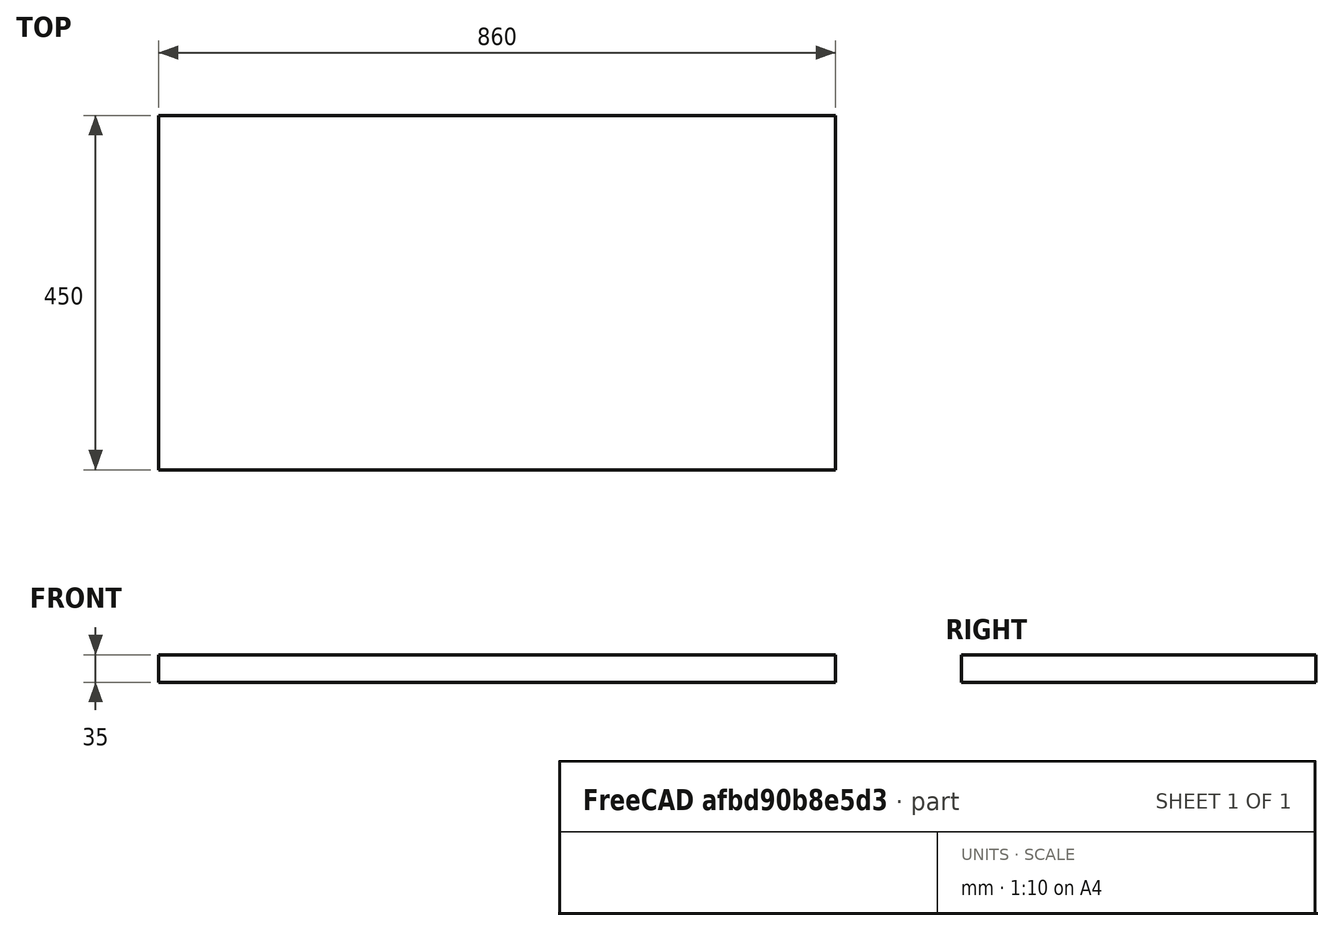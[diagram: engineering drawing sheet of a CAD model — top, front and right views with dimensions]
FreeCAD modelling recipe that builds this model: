
FCSTD DOCUMENT  (FreeCAD 0.18R4 (GitTag))
Label: benchtop_interior
License: All rights reserved
LicenseURL: http://en.wikipedia.org/wiki/All_rights_reserved
objects: Sketcher::SketchObject×1, PartDesign::Pad×1, PartDesign::Body×1
note: 4 computed .brp shape members not serialized (recipe doc carries the construction recipe); baked Part::Feature solids carry a one-line shape summary decoded from their .brp

FEATURE [Sketcher::SketchObject] Sketch
  MapMode = 5
  Placement = pos=(0,0,0) rot=(0.57735,0.57735,0.57735;2.0944rad)
  Support = -> [YZ_Plane]
  sketch-geometry (4):
    g0: LineSegment StartX=0 StartY=0 StartZ=0 EndX=-450 EndY=0 EndZ=0
    g1: LineSegment StartX=-450 StartY=0 StartZ=0 EndX=-450 EndY=35 EndZ=0
    g2: LineSegment StartX=-450 StartY=35 StartZ=0 EndX=0 EndY=35 EndZ=0
    g3: LineSegment StartX=0 StartY=35 StartZ=0 EndX=0 EndY=0 EndZ=0
  constraints (11):
    c: Coincident(g0,g1)
    c: Coincident(g1,g2)
    c: Coincident(g2,g3)
    c: Coincident(g3,g0)
    c: Horizontal(g0)
    c: Horizontal(g2)
    c: Vertical(g1)
    c: Vertical(g3)
    c: Coincident(g0,g-1)
    c: DistanceY(g3,g3) = 35
    c: DistanceX(g0,g0) = 450
FEATURE [PartDesign::Pad] Pad
  Length = 860
  Length2 = 100
  Placement = pos=(0,0,0) rot=(0.57735,0.57735,0.57735;2.0944rad)
  Profile = -> Sketch
  Type = 0
FEATURE [PartDesign::Body] Body
  Group = -> [Sketch,Pad]
  Origin = -> Origin
  Tip = -> Pad
